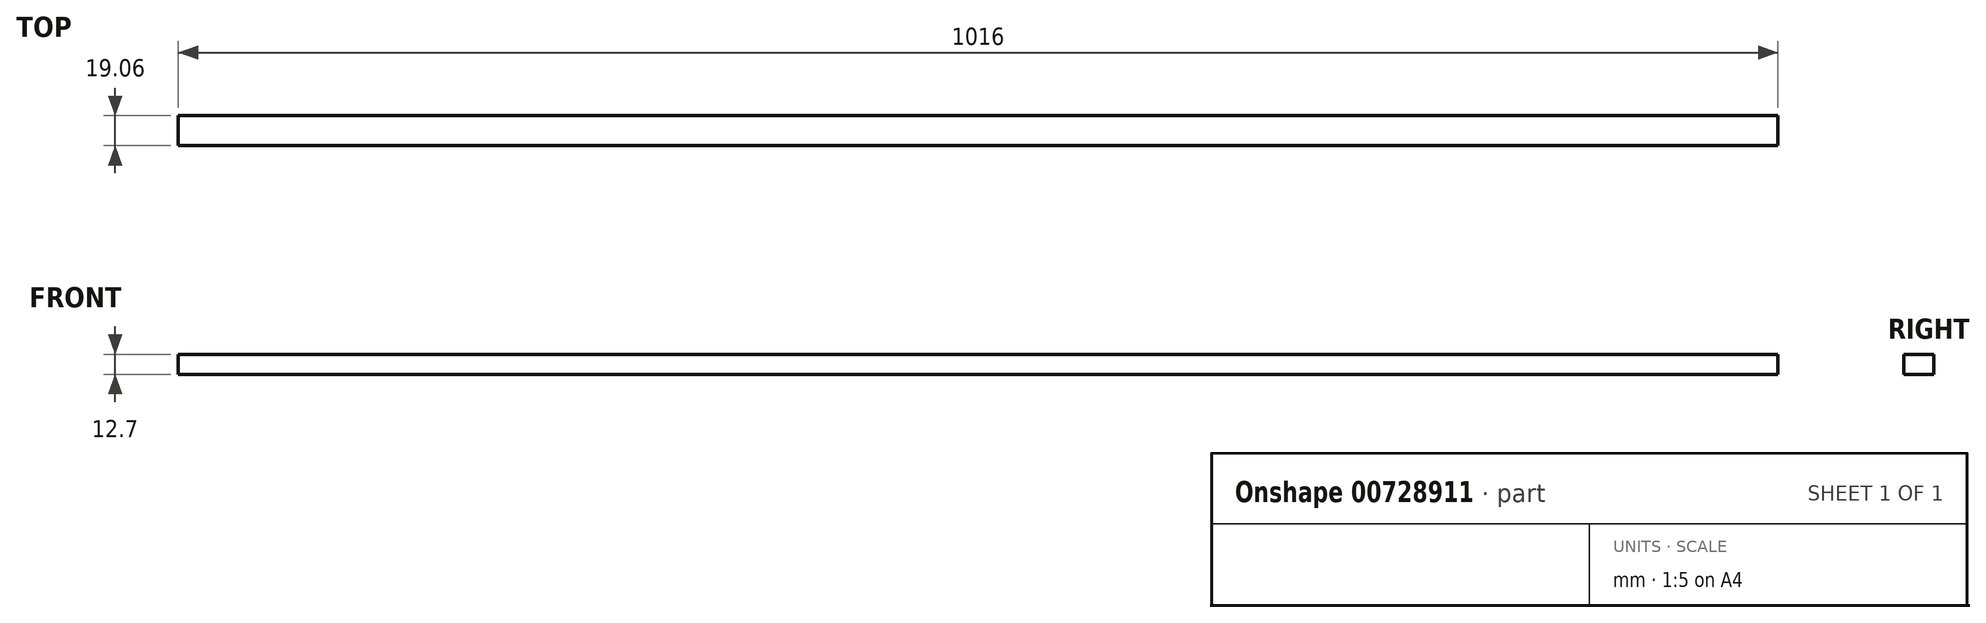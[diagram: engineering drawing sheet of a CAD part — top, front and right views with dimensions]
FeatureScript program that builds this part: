
annotation { "Feature Type Name" : "Feature", "Feature Type Description" : "" }
export const myFeature = defineFeature(function(context is Context, id is Id, definition is map)
    precondition{}
    {
        {
            var Q0;
            Q0=qCreatedBy(makeId("Top.planeOp"),FACE);
            var sketch = newSketch(context, id + "F0", { "sketchPlane" : qUnion([Q0])});
            skLineSegment(sketch, "E0.bottom", {"start": v(508, -9.52) * mm, "end": v(-508, -9.53) * mm});
            skLineSegment(sketch, "E0.top", {"start": v(508, 9.53) * mm, "end": v(-508, 9.52) * mm});
            skLineSegment(sketch, "E0.left", {"start": v(508, -9.52) * mm, "end": v(508, 9.53) * mm});
            skLineSegment(sketch, "E0.right", {"start": v(-508, -9.53) * mm, "end": v(-508, 9.52) * mm});
            skPoint(sketch, "E0.middle", {"position": v(0, 0) * mm});
            skSolve(sketch);
        }
        {
            var Q0;
            Q0=makeQuery(id+"F0.imprint","IMPRINT",FACE,{"disambiguationData":[TD([[makeQuery(id+"F0.imprint","IMPRINT",EDGE,{"derivedFrom":sQuery(id+"F0.wireOp",EDGE,"E0.bottom")}),-1.0]])]});
            extrude(context, id + "F1", {"entities" : qUnion([Q0]), "oppositeDirection" : true, "depth" : 12.7 * mm, "offsetDistance" : 25.4 * mm});
        }
    });
